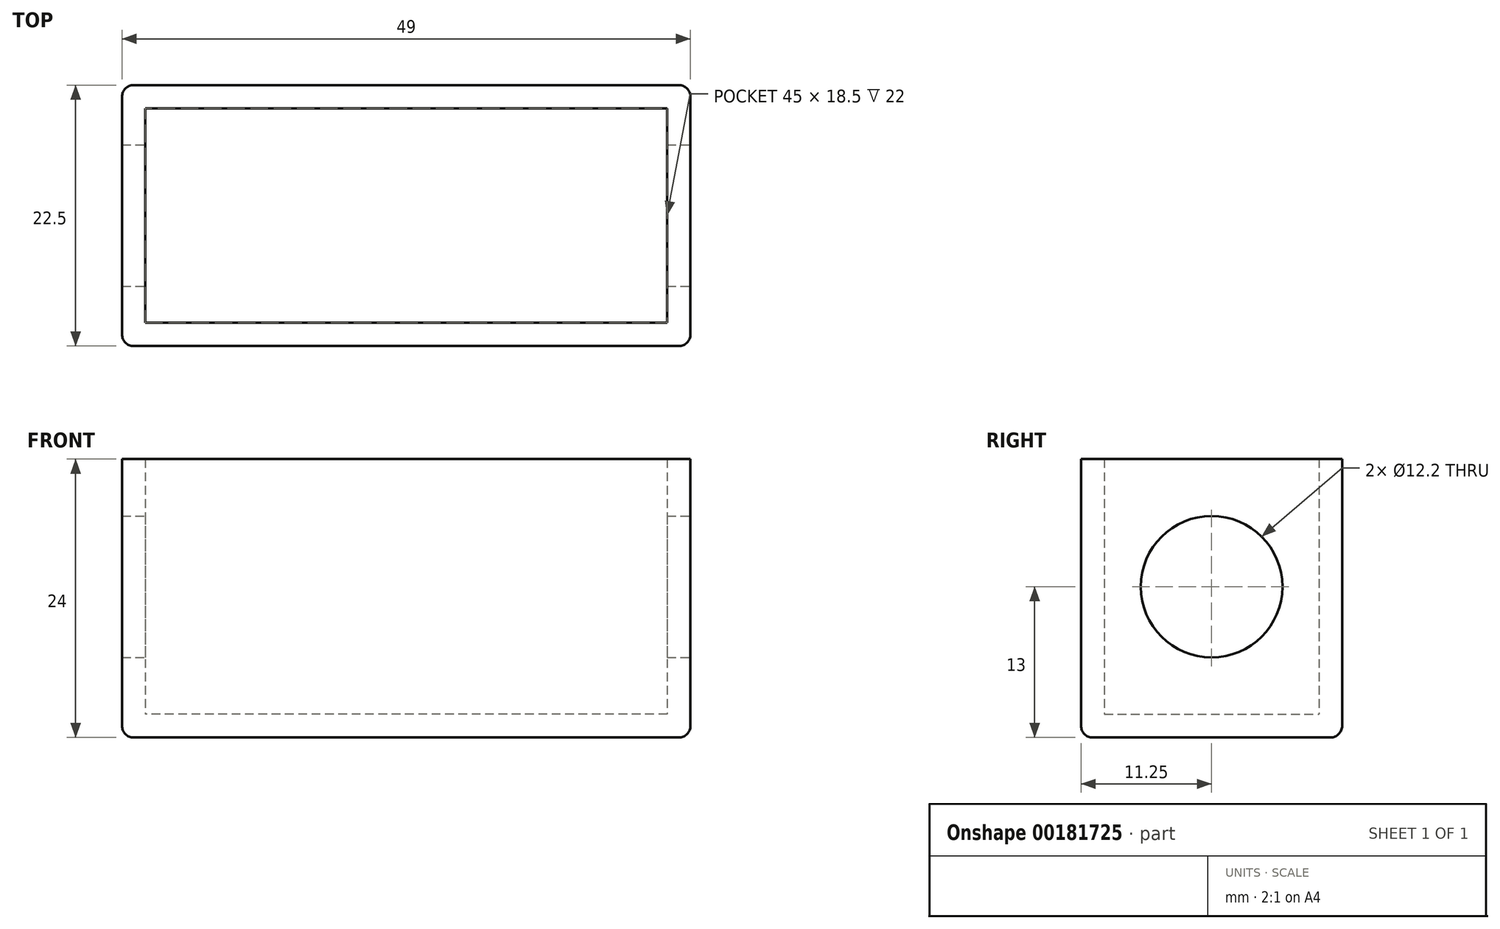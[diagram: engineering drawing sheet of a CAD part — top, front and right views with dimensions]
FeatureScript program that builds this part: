
annotation { "Feature Type Name" : "Feature", "Feature Type Description" : "" }
export const myFeature = defineFeature(function(context is Context, id is Id, definition is map)
    precondition{}
    {
        {
            var Q0;
            Q0=qCreatedBy(makeId("Top.planeOp"),FACE);
            var sketch = newSketch(context, id + "F0", { "sketchPlane" : qUnion([Q0])});
            skLineSegment(sketch, "E0.bottom", {"start": v(22.5, -9.25) * mm, "end": v(-22.5, -9.25) * mm});
            skLineSegment(sketch, "E0.top", {"start": v(22.5, 9.25) * mm, "end": v(-22.5, 9.25) * mm});
            skLineSegment(sketch, "E0.left", {"start": v(22.5, -9.25) * mm, "end": v(22.5, 9.25) * mm});
            skLineSegment(sketch, "E0.right", {"start": v(-22.5, -9.25) * mm, "end": v(-22.5, 9.25) * mm});
            skPoint(sketch, "E0.middle", {"position": v(0, 0) * mm});
            skLineSegment(sketch, "E1.0", {"start": v(24.5, 11.25) * mm, "end": v(-24.5, 11.25) * mm});
            skLineSegment(sketch, "E1.1", {"start": v(24.5, -11.25) * mm, "end": v(24.5, 11.25) * mm});
            skLineSegment(sketch, "E1.2", {"start": v(24.5, -11.25) * mm, "end": v(-24.5, -11.25) * mm});
            skLineSegment(sketch, "E1.3", {"start": v(-24.5, -11.25) * mm, "end": v(-24.5, 11.25) * mm});
            skSolve(sketch);
        }
        {
            var Q0;
            Q0 = qSketchRegion(id + "F0", true);
            extrude(context, id + "F1", {"entities" : qUnion([Q0]), "depth" : 22 * mm});
        }
        {
            var Q0;
            Q0=makeQuery(id+"F1.opExtrude","CAP_FACE",FACE,{"disambiguationData":[OSD([sQuery(id+"F0.wireOp",EDGE,"E0.bottom"),sQuery(id+"F0.wireOp",EDGE,"E0.top"),sQuery(id+"F0.wireOp",EDGE,"E0.left"),sQuery(id+"F0.wireOp",EDGE,"E0.right"),sQuery(id+"F0.wireOp",EDGE,"E1.0"),sQuery(id+"F0.wireOp",EDGE,"E1.1"),sQuery(id+"F0.wireOp",EDGE,"E1.2"),sQuery(id+"F0.wireOp",EDGE,"E1.3")])],"isStart":true});
            var sketch = newSketch(context, id + "F2", { "sketchPlane" : qUnion([Q0])});
            skLineSegment(sketch, "E2.bottom", {"start": v(-24.5, -11.25) * mm, "end": v(24.5, -11.25) * mm});
            skLineSegment(sketch, "E2.top", {"start": v(-24.5, 11.25) * mm, "end": v(24.5, 11.25) * mm});
            skLineSegment(sketch, "E2.left", {"start": v(-24.5, -11.25) * mm, "end": v(-24.5, 11.25) * mm});
            skLineSegment(sketch, "E2.right", {"start": v(24.5, -11.25) * mm, "end": v(24.5, 11.25) * mm});
            skSolve(sketch);
        }
        {
            var Q0;
            Q0 = qSketchRegion(id + "F2", true);
            extrude(context, id + "F3", {"entities" : qUnion([Q0]), "operationType" : NewBodyOperationType.ADD, "depth" : 2 * mm});
        }
        {
            var Q0;
            Q0=makeQuery(id+"F3.boolean.opBoolean","MERGE",FACE,{"derivedFrom":[makeQuery(id+"F1.opExtrude","SWEPT_FACE",FACE,{"disambiguationData":[OSD([sQuery(id+"F0.wireOp",EDGE,"E1.1")])]}),makeQuery(id+"F3.opExtrude","SWEPT_FACE",FACE,{"disambiguationData":[OSD([sQuery(id+"F2.wireOp",EDGE,"E2.right")])]})]});
            var sketch = newSketch(context, id + "F4", { "sketchPlane" : qUnion([Q0])});
            skLineSegment(sketch, "E3", {"start": v(0, 22) * mm, "end": v(0, 0) * mm, "construction": true});
            skCircle(sketch, "E4", {"center": v(0, 11) * mm, "radius": 6.1 * mm});
            skSolve(sketch);
        }
        {
            var Q0;
            Q0 = qSketchRegion(id + "F4", true);
            extrude(context, id + "F5", {"entities" : qUnion([Q0]), "operationType" : NewBodyOperationType.REMOVE, "endBound" : BoundingType.THROUGH_ALL, "oppositeDirection" : true, "depth" : 25 * mm});
        }
        {
            var Q0;
            Q0=makeQuery(id+"F3.boolean.opBoolean","MERGE",EDGE,{"derivedFrom":[makeQuery(id+"F1.opExtrude","SWEPT_EDGE",EDGE,{"disambiguationData":[OSD([sQuery(id+"F0.wireOp",EDGE,"E1.1"),sQuery(id+"F0.wireOp",EDGE,"E1.2")])]}),makeQuery(id+"F3.opExtrude","SWEPT_EDGE",EDGE,{"disambiguationData":[OSD([sQuery(id+"F2.wireOp",EDGE,"E2.top"),sQuery(id+"F2.wireOp",EDGE,"E2.right")])]})]});
            var Q1;
            Q1=makeQuery(id+"F3.boolean.opBoolean","MERGE",EDGE,{"derivedFrom":[makeQuery(id+"F1.opExtrude","SWEPT_EDGE",EDGE,{"disambiguationData":[OSD([sQuery(id+"F0.wireOp",EDGE,"E1.0"),sQuery(id+"F0.wireOp",EDGE,"E1.1")])]}),makeQuery(id+"F3.opExtrude","SWEPT_EDGE",EDGE,{"disambiguationData":[OSD([sQuery(id+"F2.wireOp",EDGE,"E2.bottom"),sQuery(id+"F2.wireOp",EDGE,"E2.right")])]})]});
            var Q2;
            Q2=makeQuery(id+"F3.opExtrude","CAP_EDGE",EDGE,{"disambiguationData":[OSD([sQuery(id+"F2.wireOp",EDGE,"E2.right")])],"isStart":false});
            var Q3;
            Q3=makeQuery(id+"F3.opExtrude","CAP_EDGE",EDGE,{"disambiguationData":[OSD([sQuery(id+"F2.wireOp",EDGE,"E2.bottom")])],"isStart":false});
            var Q4;
            Q4=makeQuery(id+"F3.opExtrude","CAP_EDGE",EDGE,{"disambiguationData":[OSD([sQuery(id+"F2.wireOp",EDGE,"E2.top")])],"isStart":false});
            var Q5;
            Q5=makeQuery(id+"F3.boolean.opBoolean","MERGE",EDGE,{"derivedFrom":[makeQuery(id+"F1.opExtrude","SWEPT_EDGE",EDGE,{"disambiguationData":[OSD([sQuery(id+"F0.wireOp",EDGE,"E1.2"),sQuery(id+"F0.wireOp",EDGE,"E1.3")])]}),makeQuery(id+"F3.opExtrude","SWEPT_EDGE",EDGE,{"disambiguationData":[OSD([sQuery(id+"F2.wireOp",EDGE,"E2.top"),sQuery(id+"F2.wireOp",EDGE,"E2.left")])]})]});
            var Q6;
            Q6=makeQuery(id+"F3.opExtrude","CAP_EDGE",EDGE,{"disambiguationData":[OSD([sQuery(id+"F2.wireOp",EDGE,"E2.left")])],"isStart":false});
            var Q7;
            Q7=makeQuery(id+"F3.boolean.opBoolean","MERGE",EDGE,{"derivedFrom":[makeQuery(id+"F1.opExtrude","SWEPT_EDGE",EDGE,{"disambiguationData":[OSD([sQuery(id+"F0.wireOp",EDGE,"E1.0"),sQuery(id+"F0.wireOp",EDGE,"E1.3")])]}),makeQuery(id+"F3.opExtrude","SWEPT_EDGE",EDGE,{"disambiguationData":[OSD([sQuery(id+"F2.wireOp",EDGE,"E2.bottom"),sQuery(id+"F2.wireOp",EDGE,"E2.left")])]})]});
            fillet(context, id + "F6", {"entities" : qUnion([Q0, Q1, Q2, Q3, Q4, Q5, Q6, Q7]), "radius" : 1 * mm, "tangentPropagation" : true, "allowEdgeOverflow" : false});
        }
    });
